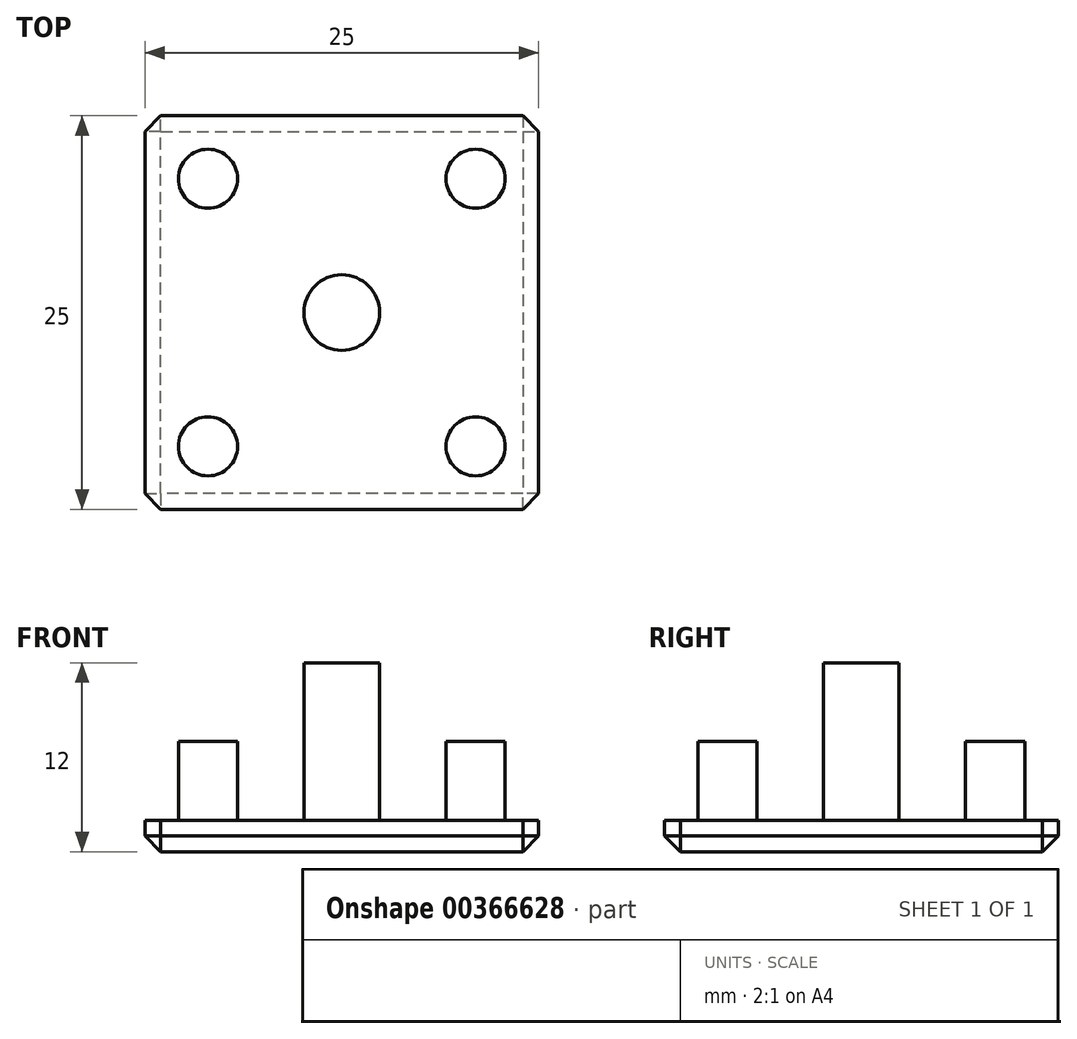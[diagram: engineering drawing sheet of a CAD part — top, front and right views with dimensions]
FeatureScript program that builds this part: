
annotation { "Feature Type Name" : "Feature", "Feature Type Description" : "" }
export const myFeature = defineFeature(function(context is Context, id is Id, definition is map)
    precondition{}
    {
        {
            var Q0;
            Q0=qCreatedBy(makeId("Top.planeOp"),FACE);
            var sketch = newSketch(context, id + "F0", { "sketchPlane" : qUnion([Q0])});
            skLineSegment(sketch, "E0.bottom", {"start": v(12.5, -12.5) * mm, "end": v(-12.5, -12.5) * mm});
            skLineSegment(sketch, "E0.top", {"start": v(12.5, 12.5) * mm, "end": v(-12.5, 12.5) * mm});
            skLineSegment(sketch, "E0.left", {"start": v(12.5, -12.5) * mm, "end": v(12.5, 12.5) * mm});
            skLineSegment(sketch, "E0.right", {"start": v(-12.5, -12.5) * mm, "end": v(-12.5, 12.5) * mm});
            skPoint(sketch, "E0.middle", {"position": v(0, 0) * mm});
            skSolve(sketch);
        }
        {
            var Q0;
            Q0 = qSketchRegion(id + "F0", true);
            extrude(context, id + "F1", {"entities" : qUnion([Q0]), "depth" : 2 * mm, "offsetDistance" : 25 * mm});
        }
        {
            var Q0;
            Q0=makeQuery(id+"F1.opExtrude","CAP_FACE",FACE,{"disambiguationData":[OSD([sQuery(id+"F0.wireOp",EDGE,"E0.bottom"),sQuery(id+"F0.wireOp",EDGE,"E0.top"),sQuery(id+"F0.wireOp",EDGE,"E0.left"),sQuery(id+"F0.wireOp",EDGE,"E0.right")])],"isStart":false});
            var sketch = newSketch(context, id + "F2", { "sketchPlane" : qUnion([Q0])});
            skCircle(sketch, "E1", {"center": v(0, 0) * mm, "radius": 2.4 * mm});
            skSolve(sketch);
        }
        {
            var Q0;
            Q0 = qSketchRegion(id + "F2", true);
            extrude(context, id + "F3", {"entities" : qUnion([Q0]), "operationType" : NewBodyOperationType.ADD, "depth" : 10 * mm, "offsetDistance" : 25 * mm});
        }
        {
            var Q0;
            Q0=makeQuery(id+"F1.opExtrude","CAP_FACE",FACE,{"disambiguationData":[OSD([sQuery(id+"F0.wireOp",EDGE,"E0.bottom"),sQuery(id+"F0.wireOp",EDGE,"E0.top"),sQuery(id+"F0.wireOp",EDGE,"E0.left"),sQuery(id+"F0.wireOp",EDGE,"E0.right")])],"isStart":false});
            var sketch = newSketch(context, id + "F4", { "sketchPlane" : qUnion([Q0])});
            skLineSegment(sketch, "E2.bottom", {"start": v(8.5, 8.5) * mm, "end": v(-8.5, 8.5) * mm, "construction": true});
            skLineSegment(sketch, "E2.top", {"start": v(8.5, -8.5) * mm, "end": v(-8.5, -8.5) * mm, "construction": true});
            skLineSegment(sketch, "E2.left", {"start": v(8.5, 8.5) * mm, "end": v(8.5, -8.5) * mm, "construction": true});
            skLineSegment(sketch, "E2.right", {"start": v(-8.5, 8.5) * mm, "end": v(-8.5, -8.5) * mm, "construction": true});
            skPoint(sketch, "E2.middle", {"position": v(0, 0) * mm});
            skCircle(sketch, "E3", {"center": v(-8.5, 8.5) * mm, "radius": 1.88 * mm});
            skCircle(sketch, "E4", {"center": v(8.5, 8.5) * mm, "radius": 1.88 * mm});
            skCircle(sketch, "E5", {"center": v(8.5, -8.5) * mm, "radius": 1.88 * mm});
            skCircle(sketch, "E6", {"center": v(-8.5, -8.5) * mm, "radius": 1.88 * mm});
            skSolve(sketch);
        }
        {
            var Q0;
            Q0 = qSketchRegion(id + "F4", true);
            extrude(context, id + "F5", {"entities" : qUnion([Q0]), "operationType" : NewBodyOperationType.ADD, "depth" : 5 * mm, "offsetDistance" : 25 * mm});
        }
        {
            var Q0;
            Q0=makeQuery(id+"F1.opExtrude","CAP_FACE",FACE,{"disambiguationData":[OSD([sQuery(id+"F0.wireOp",EDGE,"E0.bottom"),sQuery(id+"F0.wireOp",EDGE,"E0.top"),sQuery(id+"F0.wireOp",EDGE,"E0.left"),sQuery(id+"F0.wireOp",EDGE,"E0.right")])],"isStart":true});
            var Q1;
            Q1=makeQuery(id+"F1.opExtrude","SWEPT_EDGE",EDGE,{"disambiguationData":[OSD([sQuery(id+"F0.wireOp",EDGE,"E0.bottom"),sQuery(id+"F0.wireOp",EDGE,"E0.right")])]});
            var Q2;
            Q2=makeQuery(id+"F1.opExtrude","SWEPT_EDGE",EDGE,{"disambiguationData":[OSD([sQuery(id+"F0.wireOp",EDGE,"E0.bottom"),sQuery(id+"F0.wireOp",EDGE,"E0.left")])]});
            var Q3;
            Q3=makeQuery(id+"F1.opExtrude","SWEPT_EDGE",EDGE,{"disambiguationData":[OSD([sQuery(id+"F0.wireOp",EDGE,"E0.top"),sQuery(id+"F0.wireOp",EDGE,"E0.left")])]});
            var Q4;
            Q4=makeQuery(id+"F1.opExtrude","SWEPT_EDGE",EDGE,{"disambiguationData":[OSD([sQuery(id+"F0.wireOp",EDGE,"E0.top"),sQuery(id+"F0.wireOp",EDGE,"E0.right")])]});
            chamfer(context, id + "F6", {"entities" : qUnion([Q0, Q1, Q2, Q3, Q4]), "width" : 1 * mm, "tangentPropagation" : true});
        }
    });
